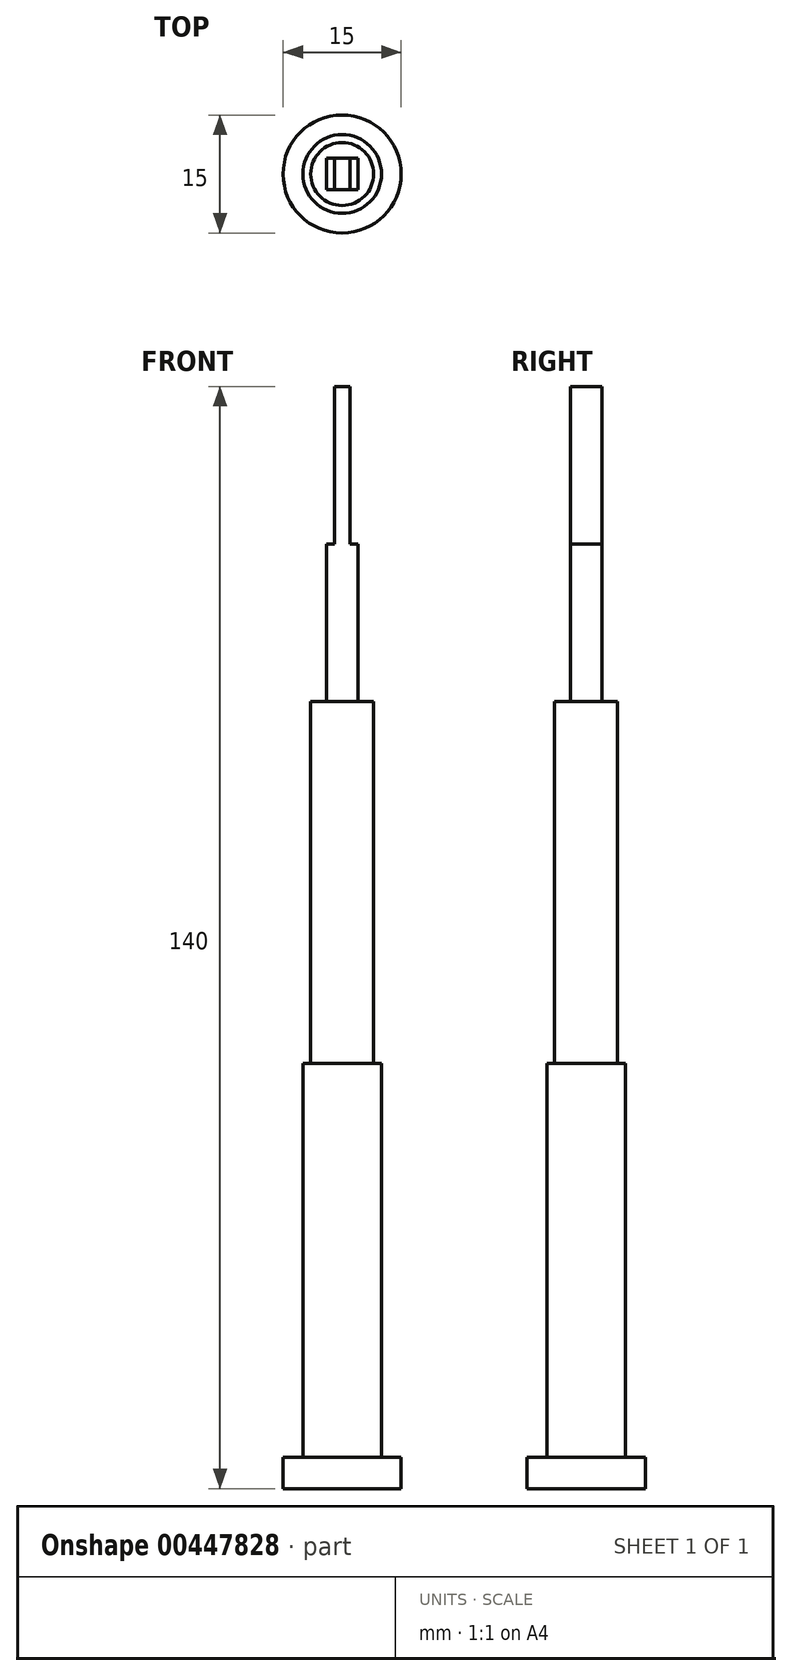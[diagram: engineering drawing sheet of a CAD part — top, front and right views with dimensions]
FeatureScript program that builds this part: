
annotation { "Feature Type Name" : "Feature", "Feature Type Description" : "" }
export const myFeature = defineFeature(function(context is Context, id is Id, definition is map)
    precondition{}
    {
        {
            var Q0;
            Q0=qCreatedBy(makeId("Top.planeOp"),FACE);
            var sketch = newSketch(context, id + "F0", { "sketchPlane" : qUnion([Q0])});
            skCircle(sketch, "E0", {"center": v(0, 0) * mm, "radius": 7.5 * mm});
            skSolve(sketch);
        }
        {
            var Q0;
            Q0=qSketchRegion(id+"F0",true);
            extrude(context, id + "F1", {"entities" : qUnion([Q0]), "depth" : 4 * mm});
        }
        {
            var Q0;
            Q0=qCreatedBy(makeId("Top.planeOp"),FACE);
            var sketch = newSketch(context, id + "F2", { "sketchPlane" : qUnion([Q0])});
            skCircle(sketch, "E1", {"center": v(0, 0) * mm, "radius": 5 * mm});
            skSolve(sketch);
        }
        {
            var Q0;
            Q0=qSketchRegion(id+"F2",true);
            extrude(context, id + "F3", {"entities" : qUnion([Q0]), "operationType" : NewBodyOperationType.ADD, "depth" : 54 * mm});
        }
        {
            var Q0;
            Q0=makeQuery(id+"F3.opExtrude","CAP_FACE",FACE,{"disambiguationData":[OSD([sQuery(id+"F2.wireOp",EDGE,"E1")])],"isStart":false});
            var sketch = newSketch(context, id + "F4", { "sketchPlane" : qUnion([Q0])});
            skCircle(sketch, "E2", {"center": v(0, 0) * mm, "radius": 4 * mm});
            skSolve(sketch);
        }
        {
            var Q0;
            Q0=qSketchRegion(id+"F4",true);
            extrude(context, id + "F5", {"entities" : qUnion([Q0]), "operationType" : NewBodyOperationType.ADD, "depth" : 46 * mm});
        }
        {
            var Q0;
            Q0=makeQuery(id+"F5.opExtrude","CAP_FACE",FACE,{"disambiguationData":[OSD([sQuery(id+"F4.wireOp",EDGE,"E2")])],"isStart":false});
            var sketch = newSketch(context, id + "F6", { "sketchPlane" : qUnion([Q0])});
            skLineSegment(sketch, "E3.bottom", {"start": v(-2, 2) * mm, "end": v(2, 2) * mm});
            skLineSegment(sketch, "E3.top", {"start": v(-2, -2) * mm, "end": v(2, -2) * mm});
            skLineSegment(sketch, "E3.left", {"start": v(-2, 2) * mm, "end": v(-2, -2) * mm});
            skLineSegment(sketch, "E3.right", {"start": v(2, 2) * mm, "end": v(2, -2) * mm});
            skSolve(sketch);
        }
        {
            var Q0;
            Q0=qSketchRegion(id+"F6",true);
            extrude(context, id + "F7", {"entities" : qUnion([Q0]), "operationType" : NewBodyOperationType.ADD, "depth" : 20 * mm});
        }
        {
            var Q0;
            Q0=makeQuery(id+"F7.opExtrude","CAP_FACE",FACE,{"disambiguationData":[OSD([sQuery(id+"F6.wireOp",EDGE,"E3.bottom"),sQuery(id+"F6.wireOp",EDGE,"E3.top"),sQuery(id+"F6.wireOp",EDGE,"E3.left"),sQuery(id+"F6.wireOp",EDGE,"E3.right")])],"isStart":false});
            var sketch = newSketch(context, id + "F8", { "sketchPlane" : qUnion([Q0])});
            skLineSegment(sketch, "E4.bottom", {"start": v(-1, 2) * mm, "end": v(1, 2) * mm});
            skLineSegment(sketch, "E4.top", {"start": v(-1, -2) * mm, "end": v(1, -2) * mm});
            skLineSegment(sketch, "E4.left", {"start": v(-1, 2) * mm, "end": v(-1, -2) * mm});
            skLineSegment(sketch, "E4.right", {"start": v(1, 2) * mm, "end": v(1, -2) * mm});
            skSolve(sketch);
        }
        {
            var Q0;
            Q0=qSketchRegion(id+"F8",true);
            extrude(context, id + "F9", {"entities" : qUnion([Q0]), "operationType" : NewBodyOperationType.ADD, "depth" : 20 * mm});
        }
    });
